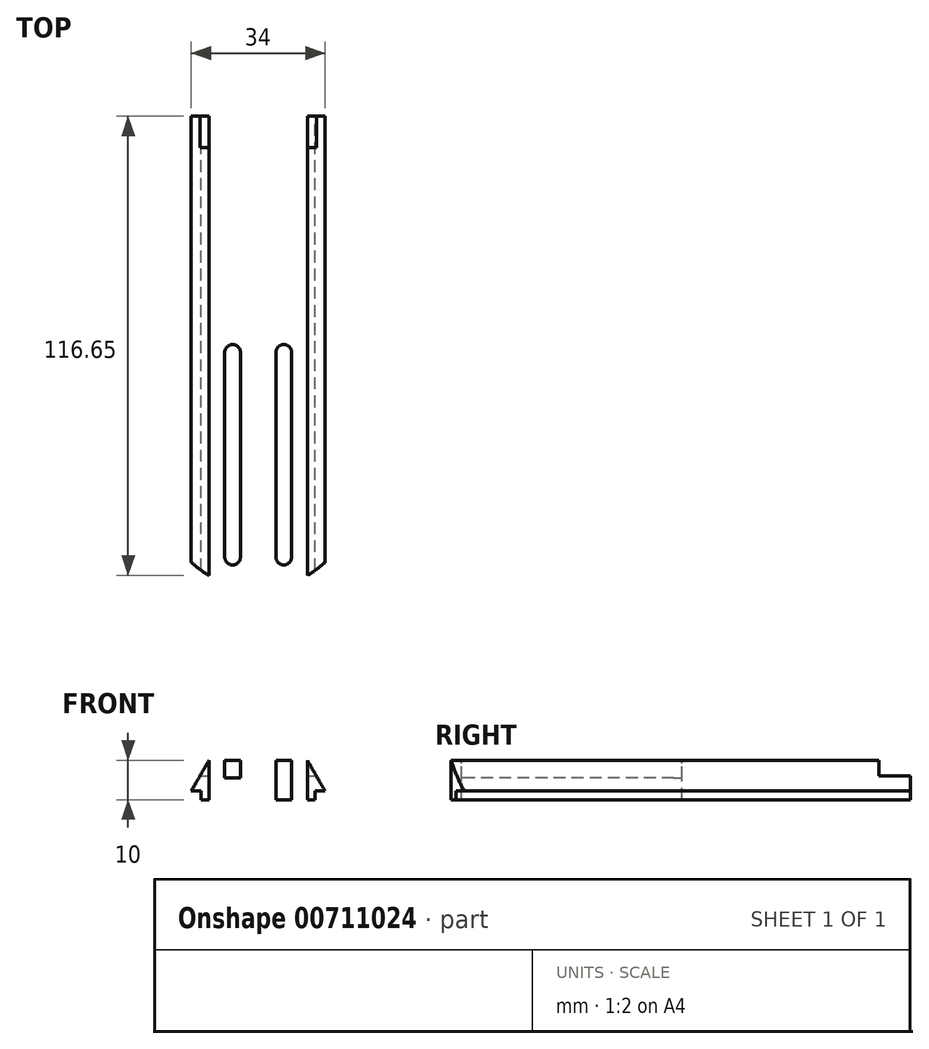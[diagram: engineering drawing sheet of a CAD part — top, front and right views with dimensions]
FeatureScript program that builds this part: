
annotation { "Feature Type Name" : "Feature", "Feature Type Description" : "" }
export const myFeature = defineFeature(function(context is Context, id is Id, definition is map)
    precondition{}
    {
        {
            var Q0;
            Q0=qCreatedBy(makeId("Front.planeOp"),FACE);
            var sketch = newSketch(context, id + "F0", { "sketchPlane" : qUnion([Q0])});
            skLineSegment(sketch, "E0", {"start": v(0, 0) * mm, "end": v(0, 59.72) * mm, "construction": true});
            skLineSegment(sketch, "E1", {"start": v(-14.5, 0) * mm, "end": v(-14.5, 2.2) * mm});
            skLineSegment(sketch, "E2", {"start": v(-14.5, 2.2) * mm, "end": v(-17, 2.2) * mm});
            skLineSegment(sketch, "E3", {"start": v(-17, 2.2) * mm, "end": v(-12.5, 10) * mm});
            skLineSegment(sketch, "E4.MirrorCS", {"start": v(14.5, 0) * mm, "end": v(14.5, 2.2) * mm});
            skLineSegment(sketch, "E5.MirrorCS", {"start": v(14.5, 2.2) * mm, "end": v(17, 2.2) * mm});
            skLineSegment(sketch, "E6.MirrorCS", {"start": v(17, 2.2) * mm, "end": v(12.5, 10) * mm});
            skLineSegment(sketch, "E7", {"start": v(-12.5, 10) * mm, "end": v(12.5, 10) * mm});
            skLineSegment(sketch, "E8", {"start": v(-14.5, 0) * mm, "end": v(14.5, 0) * mm});
            skSolve(sketch);
        }
        {
            var Q0;
            Q0 = qSketchRegion(id + "F0", true);
            extrude(context, id + "F1", {"entities" : qUnion([Q0]), "endBound" : BoundingType.SYMMETRIC, "depth" : 120 * mm, "offsetDistance" : 25 * mm});
        }
        {
            var Q0;
            Q0=makeQuery(id+"F1.opExtrude","SWEPT_FACE",FACE,{"disambiguationData":[OSD([sQuery(id+"F0.wireOp",EDGE,"E7")])]});
            var sketch = newSketch(context, id + "F2", { "sketchPlane" : qUnion([Q0])});
            skLineSegment(sketch, "E9", {"start": v(0, 0) * mm, "end": v(0, -74.28) * mm, "construction": true});
            skLineSegment(sketch, "E10", {"start": v(-25.91, -52) * mm, "end": v(23.98, -52) * mm, "construction": true});
            skLineSegment(sketch, "E11", {"start": v(-6.5, 0) * mm, "end": v(-6.5, -52) * mm, "construction": true});
            skLineSegment(sketch, "E12", {"start": v(6.5, 0) * mm, "end": v(6.5, -52) * mm, "construction": true});
            skArc(sketch, "E13.0.startCap", {"start": v(-8.5, 0) * mm, "mid": v(-6.5, 2) * mm, "end": v(-4.5, 0) * mm});
            skArc(sketch, "E13.0.endCap", {"start": v(-4.5, -52) * mm, "mid": v(-6.5, -54) * mm, "end": v(-8.5, -52) * mm});
            skLineSegment(sketch, "E13.0.left", {"start": v(-4.5, 0) * mm, "end": v(-4.5, -52) * mm});
            skLineSegment(sketch, "E13.0.right", {"start": v(-8.5, 0) * mm, "end": v(-8.5, -52) * mm});
            skArc(sketch, "E13.1.startCap", {"start": v(4.5, 0) * mm, "mid": v(6.5, 2) * mm, "end": v(8.5, 0) * mm});
            skArc(sketch, "E13.1.endCap", {"start": v(8.5, -52) * mm, "mid": v(6.5, -54) * mm, "end": v(4.5, -52) * mm});
            skLineSegment(sketch, "E13.1.left", {"start": v(8.5, 0) * mm, "end": v(8.5, -52) * mm});
            skLineSegment(sketch, "E13.1.right", {"start": v(4.5, 0) * mm, "end": v(4.5, -52) * mm});
            skSolve(sketch);
        }
        {
            var Q0;
            Q0=makeQuery(id+"F2.imprint","IMPRINT",FACE,{"disambiguationData":[TD([[makeQuery(id+"F2.imprint","IMPRINT",EDGE,{"derivedFrom":sQuery(id+"F2.wireOp",EDGE,"E13.0.startCap")}),-1.0]])]});
            var Q1;
            Q1=makeQuery(id+"F2.imprint","IMPRINT",FACE,{"disambiguationData":[TD([[makeQuery(id+"F2.imprint","IMPRINT",EDGE,{"derivedFrom":sQuery(id+"F2.wireOp",EDGE,"E13.1.startCap")}),-1.0]])]});
            extrude(context, id + "F3", {"entities" : qUnion([Q0, Q1]), "operationType" : NewBodyOperationType.REMOVE, "oppositeDirection" : true, "depth" : 25 * mm, "offsetDistance" : 25 * mm});
        }
        {
            var Q0;
            Q0=makeQuery(id+"F1.opExtrude","SWEPT_FACE",FACE,{"disambiguationData":[OSD([sQuery(id+"F0.wireOp",EDGE,"E8")])]});
            var sketch = newSketch(context, id + "F4", { "sketchPlane" : qUnion([Q0])});
            skArc(sketch, "E14.0", {"start": v(8.5, 52) * mm, "mid": v(6.5, 54) * mm, "end": v(4.5, 52) * mm});
            skLineSegment(sketch, "E15.0", {"start": v(4.5, 0) * mm, "end": v(4.5, 52) * mm});
            skLineSegment(sketch, "E16.0", {"start": v(8.5, 0) * mm, "end": v(8.5, 52) * mm});
            skArc(sketch, "E17.0", {"start": v(4.5, 0) * mm, "mid": v(6.5, -2) * mm, "end": v(8.5, 0) * mm});
            skArc(sketch, "E18.0", {"start": v(-8.5, 0) * mm, "mid": v(-6.5, -2) * mm, "end": v(-4.5, 0) * mm});
            skLineSegment(sketch, "E19.0", {"start": v(-4.5, 0) * mm, "end": v(-4.5, 52) * mm});
            skLineSegment(sketch, "E20.0", {"start": v(-8.5, 0) * mm, "end": v(-8.5, 52) * mm});
            skArc(sketch, "E21.0", {"start": v(-4.5, 52) * mm, "mid": v(-6.5, 54) * mm, "end": v(-8.5, 52) * mm});
            skLineSegment(sketch, "E22.0", {"start": v(10.5, 0) * mm, "end": v(10.5, 52) * mm});
            skArc(sketch, "E22.1", {"start": v(2.5, 0) * mm, "mid": v(6.5, -4) * mm, "end": v(10.5, 0) * mm});
            skLineSegment(sketch, "E22.2", {"start": v(2.5, 0) * mm, "end": v(2.5, 52) * mm});
            skArc(sketch, "E22.3", {"start": v(10.5, 52) * mm, "mid": v(6.5, 56) * mm, "end": v(2.5, 52) * mm});
            skLineSegment(sketch, "E23.0", {"start": v(-2.5, 0) * mm, "end": v(-2.5, 52) * mm});
            skArc(sketch, "E23.1", {"start": v(-10.5, 0) * mm, "mid": v(-6.5, -4) * mm, "end": v(-2.5, 0) * mm});
            skLineSegment(sketch, "E23.2", {"start": v(-10.5, 0) * mm, "end": v(-10.5, 52) * mm});
            skArc(sketch, "E23.3", {"start": v(-2.5, 52) * mm, "mid": v(-6.5, 56) * mm, "end": v(-10.5, 52) * mm});
            skSolve(sketch);
        }
        {
            var Q0;
            Q0=makeQuery(id+"F4.imprint","IMPRINT",FACE,{"disambiguationData":[TD([[makeQuery(id+"F4.imprint","IMPRINT",EDGE,{"derivedFrom":sQuery(id+"F4.wireOp",EDGE,"E18.0")}),-1.0]])]});
            var Q1;
            Q1=makeQuery(id+"F4.imprint","IMPRINT",FACE,{"disambiguationData":[TD([[makeQuery(id+"F4.imprint","IMPRINT",EDGE,{"derivedFrom":sQuery(id+"F4.wireOp",EDGE,"E14.0")}),-1.0]])]});
            extrude(context, id + "F5", {"entities" : qUnion([Q0, Q1]), "operationType" : NewBodyOperationType.REMOVE, "oppositeDirection" : true, "depth" : 5.5 * mm, "offsetDistance" : 25 * mm});
        }
        {
            var Q0;
            Q0=makeQuery(id+"F1.opExtrude","SWEPT_FACE",FACE,{"disambiguationData":[OSD([sQuery(id+"F0.wireOp",EDGE,"E8")])]});
            var sketch = newSketch(context, id + "F6", { "sketchPlane" : qUnion([Q0])});
            skArc(sketch, "E24", {"start": v(21.2, 48.26) * mm, "mid": v(0.45, 60) * mm, "end": v(-20.7, 49) * mm});
            skPoint(sketch, "E24.centerSnap0", {"position": v(0, 60) * mm});
            skLineSegment(sketch, "E25.bottom", {"start": v(-20.7, 66.26) * mm, "end": v(21.2, 66.26) * mm});
            skLineSegment(sketch, "E25.left", {"start": v(-20.7, 66.26) * mm, "end": v(-20.7, 49) * mm});
            skLineSegment(sketch, "E25.right", {"start": v(21.2, 66.26) * mm, "end": v(21.2, 48.26) * mm});
            skSolve(sketch);
        }
        {
            var Q0;
            {var subQ0=sQuery(id+"F6.wireOp",EDGE,"E24");var subQ1=sQuery(id+"F0.wireOp",EDGE,"E8");var subQ4=makeQuery(id+"F1.opExtrude","CAP_EDGE",EDGE,{"disambiguationData":[OSD([subQ1])],"isStart":false});var subQ5=makeQuery(id+"F6.imprint","INTERSECT",VERTEX,{"derivedFrom":[subQ4,subQ0]});Q0=makeQuery(id+"F6.imprint","IMPRINT",FACE,{"disambiguationData":[TD([[makeQuery(id+"F6.imprint","IMPRINT",EDGE,{"disambiguationData":[TD([[subQ5,1.0]])],"derivedFrom":subQ0}),-1.0]])]});}
            var Q1;
            {var subQ0=sQuery(id+"F6.wireOp",EDGE,"E24");var subQ1=sQuery(id+"F0.wireOp",EDGE,"E8");var subQ4=makeQuery(id+"F1.opExtrude","CAP_EDGE",EDGE,{"disambiguationData":[OSD([subQ1])],"isStart":false});var subQ5=makeQuery(id+"F6.imprint","INTERSECT",VERTEX,{"derivedFrom":[subQ4,subQ0]});Q1=makeQuery(id+"F6.imprint","IMPRINT",FACE,{"disambiguationData":[TD([[makeQuery(id+"F6.imprint","IMPRINT",EDGE,{"disambiguationData":[TD([[subQ5,-1.0]])],"derivedFrom":subQ0}),-1.0]])]});}
            var Q2;
            Q2=makeQuery(id+"F6.imprint","IMPRINT",FACE,{"disambiguationData":[TD([[makeQuery(id+"F6.imprint","IMPRINT",EDGE,{"derivedFrom":sQuery(id+"F6.wireOp",EDGE,"E25.bottom")}),-1.0]])]});
            extrude(context, id + "F7", {"entities" : qUnion([Q0, Q1, Q2]), "operationType" : NewBodyOperationType.REMOVE, "oppositeDirection" : true, "depth" : 25 * mm, "offsetDistance" : 25 * mm});
        }
        {
            var Q0;
            Q0=makeQuery(id+"F1.opExtrude","SWEPT_FACE",FACE,{"disambiguationData":[OSD([sQuery(id+"F0.wireOp",EDGE,"E7")])]});
            var sketch = newSketch(context, id + "F8", { "sketchPlane" : qUnion([Q0])});
            skLineSegment(sketch, "E26.0", {"start": v(-12.5, 60) * mm, "end": v(12.5, 60) * mm});
            skLineSegment(sketch, "E27.bottom", {"start": v(-26.19, 60) * mm, "end": v(21.17, 60) * mm});
            skLineSegment(sketch, "E27.top", {"start": v(-26.19, 52) * mm, "end": v(21.17, 52) * mm});
            skLineSegment(sketch, "E27.left", {"start": v(-26.19, 60) * mm, "end": v(-26.19, 52) * mm});
            skLineSegment(sketch, "E27.right", {"start": v(21.17, 60) * mm, "end": v(21.17, 52) * mm});
            skSolve(sketch);
        }
        {
            var Q0;
            Q0 = qSketchRegion(id + "F8", true);
            extrude(context, id + "F9", {"entities" : qUnion([Q0]), "operationType" : NewBodyOperationType.REMOVE, "oppositeDirection" : true, "depth" : 4 * mm, "offsetDistance" : 25 * mm});
        }
        {
            var Q0;
            Q0=makeQuery(id+"F9.boolean.opBoolean","COPY",FACE,{"derivedFrom":makeQuery(id+"F9.opExtrude","CAP_FACE",FACE,{"disambiguationData":[OSD([sQuery(id+"F8.wireOp",EDGE,"E27.bottom"),sQuery(id+"F8.wireOp",EDGE,"E27.top"),sQuery(id+"F8.wireOp",EDGE,"E27.left"),sQuery(id+"F8.wireOp",EDGE,"E27.right")])],"isStart":false})});
            var sketch = newSketch(context, id + "F10", { "sketchPlane" : qUnion([Q0])});
            skLineSegment(sketch, "E28", {"start": v(0, 60) * mm, "end": v(0, 31.65) * mm, "construction": true});
            skLineSegment(sketch, "E29", {"start": v(-14.8, 56) * mm, "end": v(20.99, 56) * mm, "construction": true});
            skPoint(sketch, "E30", {"position": v(-9, 56) * mm});
            skPoint(sketch, "E31", {"position": v(9, 56) * mm});
            skSolve(sketch);
        }
        {
            var Q0;
            Q0=sQuery(id+"F10.wireOp",VERTEX,"E31");
            var Q1;
            Q1=sQuery(id+"F10.wireOp",VERTEX,"E30");
            var Q2;
            Q2=makeQuery(id+"F1.opExtrude","SWEPT_BODY",BODY,{"disambiguationData":[OSD([sQuery(id+"F0.wireOp",EDGE,"E1"),sQuery(id+"F0.wireOp",EDGE,"E2"),sQuery(id+"F0.wireOp",EDGE,"E3"),sQuery(id+"F0.wireOp",EDGE,"E4.MirrorCS"),sQuery(id+"F0.wireOp",EDGE,"E5.MirrorCS"),sQuery(id+"F0.wireOp",EDGE,"E6.MirrorCS"),sQuery(id+"F0.wireOp",EDGE,"E7"),sQuery(id+"F0.wireOp",EDGE,"E8")])]});
            hole(context, id + "F11", {"style" : HoleStyle.SIMPLE, "endStyle" : HoleEndStyle.THROUGH, "standardTappedOrClearance" : lookupTablePath({ "standard" : "ISO", "engagement" : "75%", "pitch" : "0.5 mm", "size" : "M3", "type" : "Tapped" }), "standardBlindInLast" : lookupTablePath({ "standard" : "ISO", "engagement" : "75%", "pitch" : "0.5 mm", "size" : "M3", "type" : "Tapped" }), "holeDiameter" : 2.5 * mm, "majorDiameter" : 3 * mm, "showTappedDepth" : true, "tappedDepth" : 5.9 * mm, "tapClearance" : 3, "startFromSketch" : true, "locations" : qUnion([Q0, Q1]), "scope" : qUnion([Q2])});
        }
    });
